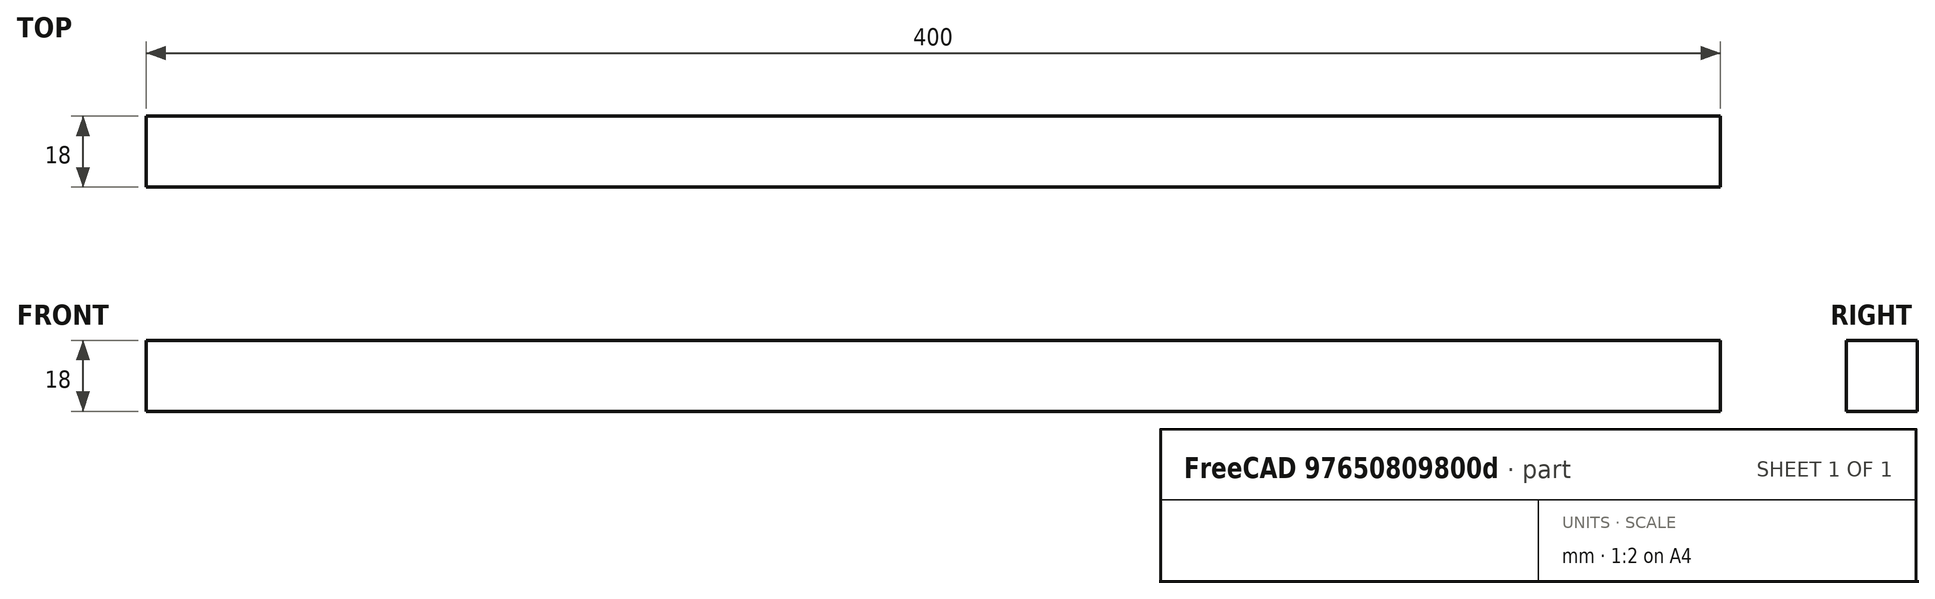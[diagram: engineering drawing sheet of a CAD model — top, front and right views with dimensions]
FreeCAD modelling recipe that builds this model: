
FCSTD DOCUMENT  (FreeCAD 0.19R24291 (Git))
Label: 3000_strut_x_18_18_30
License: All rights reserved
LicenseURL: http://en.wikipedia.org/wiki/All_rights_reserved
objects: Sketcher::SketchObject×1, PartDesign::Pad×1, PartDesign::Body×1
note: 4 computed .brp shape members not serialized (recipe doc carries the construction recipe); baked Part::Feature solids carry a one-line shape summary decoded from their .brp

FEATURE [Sketcher::SketchObject] Sketch
  FullyConstrained = true
  MapMode = 5
  Placement = pos=(0,0,0) rot=(0.57735,0.57735,0.57735;2.0944rad)
  Support = -> [YZ_Plane]
  sketch-geometry (4):
    g0: LineSegment StartX=0 StartY=18 StartZ=0 EndX=18 EndY=18 EndZ=0
    g1: LineSegment StartX=18 StartY=18 StartZ=0 EndX=18 EndY=0 EndZ=0
    g2: LineSegment StartX=18 StartY=0 StartZ=0 EndX=0 EndY=0 EndZ=0
    g3: LineSegment StartX=0 StartY=0 StartZ=0 EndX=0 EndY=18 EndZ=0
  constraints (12):
    c: Coincident(g0,g1)
    c: Coincident(g1,g2)
    c: Coincident(g2,g3)
    c: Coincident(g3,g0)
    c: Horizontal(g0)
    c: Horizontal(g2)
    c: Vertical(g1)
    c: Vertical(g3)
    c: PointOnObject(g0,g-2)
    c: PointOnObject(g1,g-1)
    c: Equal(g1,g0)
    c: DistanceY(g1,g1) = 18
FEATURE [PartDesign::Pad] Pad
  Direction = (1,1,1)
  Length = 400
  Length2 = 100
  Midplane = true
  Placement = pos=(0,0,0) rot=(0.57735,0.57735,0.57735;2.0944rad)
  Profile = -> Sketch
  Type = 0
  expr: Length = 400
FEATURE [PartDesign::Body] Body
  Group = -> [Sketch,Pad]
  Origin = -> Origin
  Tip = -> Pad
